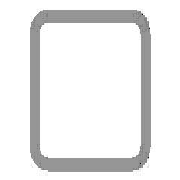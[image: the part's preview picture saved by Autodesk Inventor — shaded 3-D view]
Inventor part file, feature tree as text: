
AUTODESK INVENTOR PART (.ipt)
format: ipt  version: 2024.3 (Build 283343000, 343)  size: 147,456 bytes
history: native  units: mm (DEFAULTED — no unit token found)
features: other x4, plane x3, split x2, sketch x1
ambient origin geometry x8: Origin, YZ Plane, XZ Plane, XY Plane, X Axis, Y Axis, Z Axis, Center Point
bodies: Solid1 (feature_tree), Body (feature_tree)
feature tree (10):
  parser-record x1  (decoder bookkeeping rows leaked as tree rows — omitted from the tree; the rows remain in map.json)
  other  "Driven Length"
  other  "Start Plane"
  other  "End Plane"
  plane  "Work Plane4"
  split  "Split1"
  plane  "Work Plane5"
  split  "Split2"
  sketch  "Sketch3"  dims[d3=270.0mm d4=0.0mm d7=4.0mm d9=20.0mm d11=20.0mm d12=2.0mm d13=-10.0mm d14=260.0mm d15=10.0mm d16=10.0mm d17=90.0deg d18=270.0mm]
  plane  "Work Plane3"
